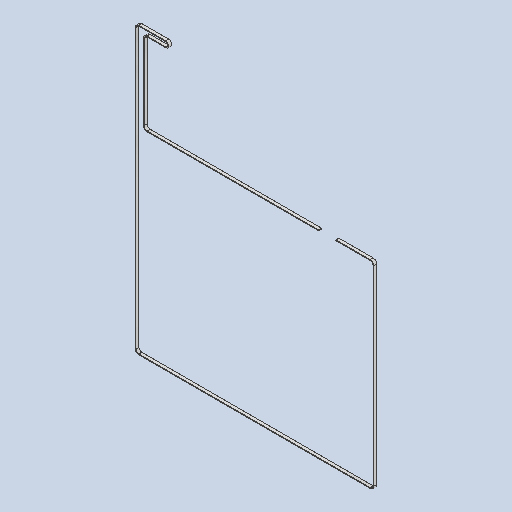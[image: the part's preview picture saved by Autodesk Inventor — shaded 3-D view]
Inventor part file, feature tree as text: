
AUTODESK INVENTOR PART (.ipt)
format: ipt  version: 2024.2 (Build 282272000, 272)  size: 107,008 bytes
history: native  units: in
note: dims shown in document units (in); Inventor stores cm internally (conversion verified against a paired STEP export)
features: sweep x1
ambient origin geometry x8: Origin, YZ Plane, XZ Plane, XY Plane, X Axis, Y Axis, Z Axis, Center Point
bodies: Solid1 (feature_tree)
feature tree (1):
  sweep  "Sweep1"
